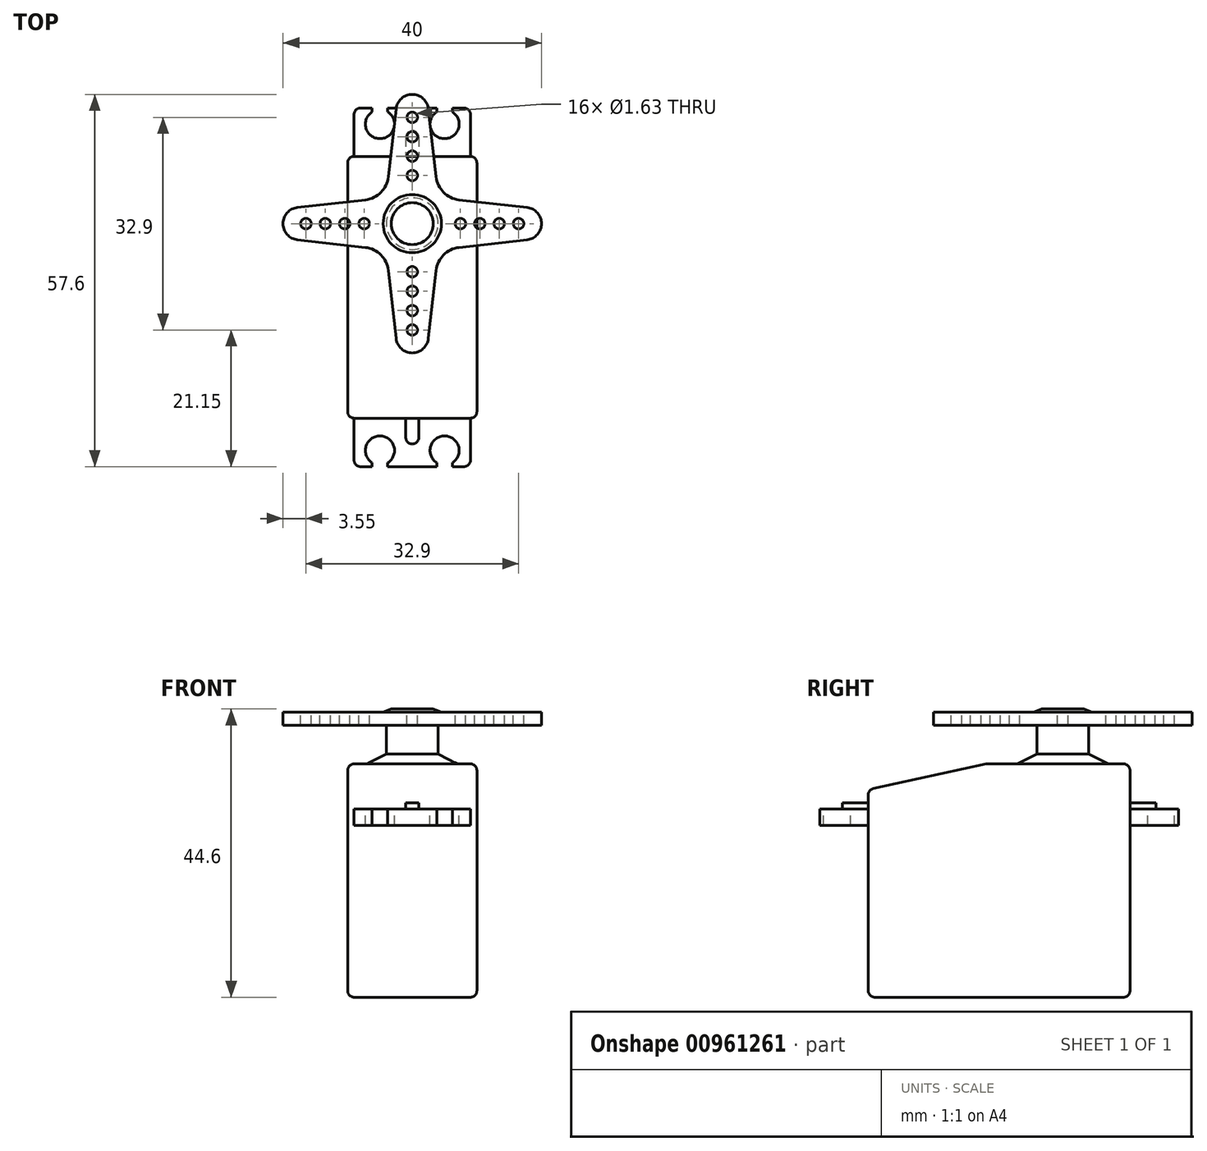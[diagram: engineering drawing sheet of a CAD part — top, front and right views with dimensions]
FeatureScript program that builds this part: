
annotation { "Feature Type Name" : "Feature", "Feature Type Description" : "" }
export const myFeature = defineFeature(function(context is Context, id is Id, definition is map)
    precondition{}
    {
        {
            var Q0;
            Q0=qCreatedBy(makeId("Right.planeOp"),FACE);
            var sketch = newSketch(context, id + "F0", { "sketchPlane" : qUnion([Q0])});
            skLineSegment(sketch, "E0.bottom", {"start": v(-20.25, 0) * mm, "end": v(20.25, 0) * mm});
            skLineSegment(sketch, "E0.top", {"start": v(-20.25, 36.1) * mm, "end": v(20.25, 36.1) * mm});
            skLineSegment(sketch, "E0.left", {"start": v(-20.25, 0) * mm, "end": v(-20.25, 36.1) * mm});
            skLineSegment(sketch, "E0.right", {"start": v(20.25, 0) * mm, "end": v(20.25, 36.1) * mm});
            skLineSegment(sketch, "E1.bottom", {"start": v(20.25, 29.1) * mm, "end": v(27.75, 29.1) * mm});
            skLineSegment(sketch, "E1.top", {"start": v(20.25, 26.6) * mm, "end": v(27.75, 26.6) * mm});
            skLineSegment(sketch, "E1.left", {"start": v(20.25, 29.1) * mm, "end": v(20.25, 26.6) * mm});
            skLineSegment(sketch, "E1.right", {"start": v(27.75, 29.1) * mm, "end": v(27.75, 26.6) * mm});
            skLineSegment(sketch, "E2.bottom", {"start": v(0, 36.1) * mm, "end": v(0, 36.1) * mm});
            skLineSegment(sketch, "E2.top", {"start": v(0, 0) * mm, "end": v(0, 0) * mm});
            skLineSegment(sketch, "E2.left", {"start": v(0, 36.1) * mm, "end": v(0, 0) * mm, "construction": true});
            skLineSegment(sketch, "E2.right", {"start": v(0, 36.1) * mm, "end": v(0, 0) * mm, "construction": true});
            skLineSegment(sketch, "E3.MirrorCS", {"start": v(-20.25, 29.1) * mm, "end": v(-27.75, 29.1) * mm});
            skLineSegment(sketch, "E4.MirrorCS", {"start": v(-27.75, 29.1) * mm, "end": v(-27.75, 26.6) * mm});
            skLineSegment(sketch, "E5.MirrorCS", {"start": v(-20.25, 26.6) * mm, "end": v(-27.75, 26.6) * mm});
            skLineSegment(sketch, "E6.MirrorCS", {"start": v(-20.25, 29.1) * mm, "end": v(-20.25, 26.6) * mm});
            skLineSegment(sketch, "E7", {"start": v(-20.25, 32.1) * mm, "end": v(-1.95, 36.1) * mm});
            skSolve(sketch);
        }
        {
            var Q0;
            {var subQ3=sQuery(id+"F0.wireOp",EDGE,"E0.bottom");Q0=makeQuery(id+"F0.imprint","IMPRINT",FACE,{"disambiguationData":[TD([[makeQuery(id+"F0.imprint","IMPRINT",EDGE,{"derivedFrom":subQ3}),1.0]])]});}
            extrude(context, id + "F1", {"entities" : qUnion([Q0]), "depth" : 20 * mm, "hasSecondDirection" : true, "secondDirectionOppositeDirection" : true, "secondDirectionDepth" : 25 * mm, "symmetric" : true});
        }
        {
            var Q0;
            Q0=makeQuery(id+"F0.imprint","IMPRINT",FACE,{"disambiguationData":[TD([[makeQuery(id+"F0.imprint","IMPRINT",EDGE,{"derivedFrom":sQuery(id+"F0.wireOp",EDGE,"E3.MirrorCS")}),1.0]])]});
            var Q1;
            Q1=makeQuery(id+"F0.imprint","IMPRINT",FACE,{"disambiguationData":[TD([[makeQuery(id+"F0.imprint","IMPRINT",EDGE,{"derivedFrom":sQuery(id+"F0.wireOp",EDGE,"E1.bottom")}),-1.0]])]});
            extrude(context, id + "F2", {"entities" : qUnion([Q0, Q1]), "operationType" : NewBodyOperationType.ADD, "depth" : 18 * mm, "symmetric" : true});
        }
        {
            var Q0;
            Q0=makeQuery(id+"F2.opExtrude","SWEPT_FACE",FACE,{"disambiguationData":[OSD([sQuery(id+"F0.wireOp",EDGE,"E3.MirrorCS")])]});
            var sketch = newSketch(context, id + "F3", { "sketchPlane" : qUnion([Q0])});
            skLineSegment(sketch, "E8.0", {"start": v(-10, -20.25) * mm, "end": v(-10, -1.95) * mm, "construction": true});
            skLineSegment(sketch, "E9.0", {"start": v(-10, -1.95) * mm, "end": v(-10, 20.25) * mm, "construction": true});
            skLineSegment(sketch, "E10.0", {"start": v(10, 20.25) * mm, "end": v(-10, 20.25) * mm, "construction": true});
            skLineSegment(sketch, "E11.0", {"start": v(10, -1.95) * mm, "end": v(10, 20.25) * mm, "construction": true});
            skLineSegment(sketch, "E12.0", {"start": v(10, -20.25) * mm, "end": v(10, -1.95) * mm, "construction": true});
            skLineSegment(sketch, "E13.0", {"start": v(10, -20.25) * mm, "end": v(-10, -20.25) * mm, "construction": true});
            skLineSegment(sketch, "E14", {"start": v(-10, -20.25) * mm, "end": v(10, 20.25) * mm, "construction": true});
            skLineSegment(sketch, "E15", {"start": v(-10, 20.25) * mm, "end": v(10, -20.25) * mm, "construction": true});
            skLineSegment(sketch, "E16", {"start": v(-10, 0) * mm, "end": v(10, 0) * mm, "construction": true});
            skPoint(sketch, "E16.endSnap0", {"position": v(0, 0) * mm});
            skLineSegment(sketch, "E17", {"start": v(0, -20.25) * mm, "end": v(0, 20.25) * mm, "construction": true});
            skCircle(sketch, "E18", {"center": v(-5, -25.25) * mm, "radius": 2.25 * mm});
            skLineSegment(sketch, "E19", {"start": v(-6.2, -27.75) * mm, "end": v(-3.8, -27.75) * mm});
            skLineSegment(sketch, "E20", {"start": v(-3.8, -27.75) * mm, "end": v(-3.8, -27.15) * mm});
            skLineSegment(sketch, "E21", {"start": v(-6.2, -27.75) * mm, "end": v(-6.2, -27.15) * mm});
            skLineSegment(sketch, "E22.MirrorCS", {"start": v(-6.2, 27.75) * mm, "end": v(-6.2, 27.15) * mm});
            skLineSegment(sketch, "E23.MirrorCS", {"start": v(-6.2, 27.75) * mm, "end": v(-3.8, 27.75) * mm});
            skLineSegment(sketch, "E24.MirrorCS", {"start": v(-3.8, 27.75) * mm, "end": v(-3.8, 27.15) * mm});
            skCircle(sketch, "E25.MirrorC", {"center": v(-5, 25.25) * mm, "radius": 2.25 * mm});
            skLineSegment(sketch, "E26.MirrorCS", {"start": v(3.8, -27.75) * mm, "end": v(3.8, -27.15) * mm});
            skLineSegment(sketch, "E27.MirrorCS", {"start": v(3.8, 27.75) * mm, "end": v(3.8, 27.15) * mm});
            skLineSegment(sketch, "E28.MirrorCS", {"start": v(6.2, 27.75) * mm, "end": v(6.2, 27.15) * mm});
            skLineSegment(sketch, "E29.MirrorCS", {"start": v(6.2, -27.75) * mm, "end": v(6.2, -27.15) * mm});
            skLineSegment(sketch, "E30.MirrorCS", {"start": v(6.2, 27.75) * mm, "end": v(3.8, 27.75) * mm});
            skLineSegment(sketch, "E31.MirrorCS", {"start": v(6.2, -27.75) * mm, "end": v(3.8, -27.75) * mm});
            skCircle(sketch, "E32.MirrorC", {"center": v(5, 25.25) * mm, "radius": 2.25 * mm});
            skCircle(sketch, "E33.MirrorC", {"center": v(5, -25.25) * mm, "radius": 2.25 * mm});
            skSolve(sketch);
        }
        {
            var Q0;
            Q0=qSketchRegion(id+"F3",true);
            extrude(context, id + "F4", {"entities" : qUnion([Q0]), "operationType" : NewBodyOperationType.REMOVE, "oppositeDirection" : true, "depth" : 25 * mm});
        }
        {
            var Q0;
            Q0=makeQuery(id+"F2.opExtrude","SWEPT_FACE",FACE,{"disambiguationData":[OSD([sQuery(id+"F0.wireOp",EDGE,"E3.MirrorCS")])]});
            var sketch = newSketch(context, id + "F5", { "sketchPlane" : qUnion([Q0])});
            skLineSegment(sketch, "E34.0", {"start": v(10, -20.25) * mm, "end": v(-10, -20.25) * mm, "construction": true});
            skLineSegment(sketch, "E35.0", {"start": v(10, 20.25) * mm, "end": v(-10, 20.25) * mm, "construction": true});
            skLineSegment(sketch, "E36", {"start": v(0, -20.25) * mm, "end": v(0, 20.25) * mm, "construction": true});
            skLineSegment(sketch, "E37.rect.bottom", {"start": v(1, 23.25) * mm, "end": v(-1, 23.25) * mm});
            skLineSegment(sketch, "E37.rect.top", {"start": v(1, -23.25) * mm, "end": v(-1, -23.25) * mm});
            skLineSegment(sketch, "E37.rect.left", {"start": v(1, 23.25) * mm, "end": v(1, -23.25) * mm});
            skLineSegment(sketch, "E37.rect.right", {"start": v(-1, 23.25) * mm, "end": v(-1, -23.25) * mm});
            skPoint(sketch, "E37.rect.middle", {"position": v(0, 0) * mm});
            skArc(sketch, "E38", {"start": v(1, 23.25) * mm, "mid": v(0, 24.25) * mm, "end": v(-1, 23.25) * mm});
            skArc(sketch, "E39", {"start": v(-1, -23.25) * mm, "mid": v(0, -24.25) * mm, "end": v(1, -23.25) * mm});
            skPoint(sketch, "E40", {"position": v(0, 24.25) * mm});
            skSolve(sketch);
        }
        {
            var Q0;
            Q0=qSketchRegion(id+"F5",true);
            extrude(context, id + "F6", {"entities" : qUnion([Q0]), "operationType" : NewBodyOperationType.ADD, "depth" : 1 * mm});
        }
        {
            var Q0;
            Q0=qCreatedBy(makeId("Right.planeOp"),FACE);
            var sketch = newSketch(context, id + "F7", { "sketchPlane" : qUnion([Q0])});
            skLineSegment(sketch, "E41.0", {"start": v(-1.95, 36.1) * mm, "end": v(20.25, 36.1) * mm, "construction": true});
            skLineSegment(sketch, "E42.0", {"start": v(-20.25, 0) * mm, "end": v(-20.25, 32.1) * mm, "construction": true});
            skLineSegment(sketch, "E43.0", {"start": v(20.25, 0) * mm, "end": v(20.25, 36.1) * mm, "construction": true});
            skLineSegment(sketch, "E44", {"start": v(9.85, 53.58) * mm, "end": v(9.85, 24.34) * mm, "construction": true});
            skLineSegment(sketch, "E45", {"start": v(16.85, 36.1) * mm, "end": v(13.85, 37.6) * mm});
            skLineSegment(sketch, "E46", {"start": v(13.85, 37.6) * mm, "end": v(13.85, 42.1) * mm});
            skLineSegment(sketch, "E47", {"start": v(13.85, 42.1) * mm, "end": v(29.85, 42.1) * mm});
            skLineSegment(sketch, "E48", {"start": v(29.85, 42.1) * mm, "end": v(29.85, 44.1) * mm});
            skLineSegment(sketch, "E49", {"start": v(29.85, 44.1) * mm, "end": v(14.35, 44.1) * mm});
            skLineSegment(sketch, "E50", {"start": v(14.35, 44.1) * mm, "end": v(13.1, 44.6) * mm});
            skLineSegment(sketch, "E51", {"start": v(13.1, 44.6) * mm, "end": v(9.85, 44.6) * mm});
            skLineSegment(sketch, "E52", {"start": v(9.85, 44.6) * mm, "end": v(9.85, 36.1) * mm});
            skLineSegment(sketch, "E53", {"start": v(9.85, 36.1) * mm, "end": v(16.85, 36.1) * mm});
            skSolve(sketch);
        }
        {
            var Q0;
            Q0=qSketchRegion(id+"F7",true);
            var Q1;
            Q1=sQuery(id+"F7.wireOp",EDGE,"E44");
            revolve(context, id + "F8", {"operationType" : NewBodyOperationType.ADD, "entities" : qUnion([Q0]), "axis" : qUnion([Q1]), "revolveType" : RevolveType.FULL});
        }
        {
            var Q0;
            Q0=makeQuery(id+"F8.opRevolve","SWEPT_FACE",FACE,{"disambiguationData":[OSD([sQuery(id+"F7.wireOp",EDGE,"E49")])]});
            var sketch = newSketch(context, id + "F9", { "sketchPlane" : qUnion([Q0])});
            skPoint(sketch, "E54", {"position": v(0, 9.85) * mm});
            skCircle(sketch, "E55", {"center": v(0, 17.3) * mm, "radius": 0.81 * mm});
            skCircle(sketch, "E56", {"center": v(0, 20.3) * mm, "radius": 0.81 * mm});
            skCircle(sketch, "E57", {"center": v(0, 23.3) * mm, "radius": 0.81 * mm});
            skCircle(sketch, "E58", {"center": v(0, 26.3) * mm, "radius": 0.81 * mm});
            skCircle(sketch, "E59.1.0", {"center": v(-16.45, 9.85) * mm, "radius": 0.81 * mm});
            skCircle(sketch, "E59.1.1", {"center": v(-13.45, 9.85) * mm, "radius": 0.81 * mm});
            skCircle(sketch, "E59.1.2", {"center": v(-10.45, 9.85) * mm, "radius": 0.81 * mm});
            skCircle(sketch, "E59.1.3", {"center": v(-7.45, 9.85) * mm, "radius": 0.81 * mm});
            skCircle(sketch, "E59.2.0", {"center": v(0, -6.6) * mm, "radius": 0.81 * mm});
            skCircle(sketch, "E59.2.1", {"center": v(0, -3.6) * mm, "radius": 0.81 * mm});
            skCircle(sketch, "E59.2.2", {"center": v(0, -0.6) * mm, "radius": 0.81 * mm});
            skCircle(sketch, "E59.2.3", {"center": v(0, 2.4) * mm, "radius": 0.81 * mm});
            skCircle(sketch, "E59.3.0", {"center": v(16.45, 9.85) * mm, "radius": 0.81 * mm});
            skCircle(sketch, "E59.3.1", {"center": v(13.45, 9.85) * mm, "radius": 0.81 * mm});
            skCircle(sketch, "E59.3.2", {"center": v(10.45, 9.85) * mm, "radius": 0.81 * mm});
            skCircle(sketch, "E59.3.3", {"center": v(7.45, 9.85) * mm, "radius": 0.81 * mm});
            skSolve(sketch);
        }
        {
            var Q0;
            Q0=qSketchRegion(id+"F9",true);
            extrude(context, id + "F10", {"entities" : qUnion([Q0]), "operationType" : NewBodyOperationType.REMOVE, "endBound" : BoundingType.UP_TO_NEXT, "oppositeDirection" : true, "depth" : 25 * mm});
        }
        {
            var Q0;
            Q0=makeQuery(id+"F8.opRevolve","SWEPT_FACE",FACE,{"disambiguationData":[OSD([sQuery(id+"F7.wireOp",EDGE,"E49")])]});
            var sketch = newSketch(context, id + "F11", { "sketchPlane" : qUnion([Q0])});
            skPoint(sketch, "E60", {"position": v(0, 9.85) * mm});
            skLineSegment(sketch, "E61", {"start": v(0, 9.85) * mm, "end": v(0, 29.85) * mm, "construction": true});
            skLineSegment(sketch, "E62", {"start": v(0, 9.85) * mm, "end": v(-14.14, 24) * mm, "construction": true});
            skLineSegment(sketch, "E63", {"start": v(0, 9.85) * mm, "end": v(14.14, 24) * mm, "construction": true});
            skLineSegment(sketch, "E64", {"start": v(-3.69, 17.1) * mm, "end": v(-2.5, 27.62) * mm});
            skArc(sketch, "E65", {"start": v(0, 29.85) * mm, "mid": v(-1.68, 29.21) * mm, "end": v(-2.5, 27.62) * mm});
            skArc(sketch, "E66", {"start": v(-4.84, 14.7) * mm, "mid": v(-4.06, 15.8) * mm, "end": v(-3.69, 17.1) * mm});
            skArc(sketch, "E67.MirrorCS", {"start": v(4.84, 14.7) * mm, "mid": v(4.06, 15.8) * mm, "end": v(3.69, 17.1) * mm});
            skLineSegment(sketch, "E68.MirrorCS", {"start": v(3.69, 17.1) * mm, "end": v(2.5, 27.62) * mm});
            skArc(sketch, "E69.MirrorCS", {"start": v(0, 29.85) * mm, "mid": v(1.68, 29.21) * mm, "end": v(2.5, 27.62) * mm});
            skArc(sketch, "E70.1.0", {"start": v(-4.84, 5) * mm, "mid": v(-5.95, 5.79) * mm, "end": v(-7.24, 6.16) * mm});
            skLineSegment(sketch, "E70.1.1", {"start": v(-7.24, 6.16) * mm, "end": v(-17.77, 7.35) * mm});
            skArc(sketch, "E70.1.2", {"start": v(-20, 9.85) * mm, "mid": v(-19.36, 8.17) * mm, "end": v(-17.77, 7.35) * mm});
            skArc(sketch, "E70.1.3", {"start": v(-20, 9.85) * mm, "mid": v(-19.36, 11.53) * mm, "end": v(-17.77, 12.35) * mm});
            skLineSegment(sketch, "E70.1.4", {"start": v(-7.24, 13.54) * mm, "end": v(-17.77, 12.35) * mm});
            skArc(sketch, "E70.1.5", {"start": v(-4.84, 14.7) * mm, "mid": v(-5.95, 13.91) * mm, "end": v(-7.24, 13.54) * mm});
            skArc(sketch, "E70.2.0", {"start": v(4.84, 5) * mm, "mid": v(4.06, 3.9) * mm, "end": v(3.69, 2.6) * mm});
            skLineSegment(sketch, "E70.2.1", {"start": v(3.69, 2.6) * mm, "end": v(2.5, -7.92) * mm});
            skArc(sketch, "E70.2.2", {"start": v(0, -10.15) * mm, "mid": v(1.68, -9.51) * mm, "end": v(2.5, -7.92) * mm});
            skArc(sketch, "E70.2.3", {"start": v(0, -10.15) * mm, "mid": v(-1.68, -9.51) * mm, "end": v(-2.5, -7.92) * mm});
            skLineSegment(sketch, "E70.2.4", {"start": v(-3.69, 2.6) * mm, "end": v(-2.5, -7.92) * mm});
            skArc(sketch, "E70.2.5", {"start": v(-4.84, 5) * mm, "mid": v(-4.06, 3.9) * mm, "end": v(-3.69, 2.6) * mm});
            skArc(sketch, "E70.3.0", {"start": v(4.84, 14.7) * mm, "mid": v(5.95, 13.91) * mm, "end": v(7.24, 13.54) * mm});
            skLineSegment(sketch, "E70.3.1", {"start": v(7.24, 13.54) * mm, "end": v(17.77, 12.35) * mm});
            skArc(sketch, "E70.3.2", {"start": v(20, 9.85) * mm, "mid": v(19.36, 11.53) * mm, "end": v(17.77, 12.35) * mm});
            skArc(sketch, "E70.3.3", {"start": v(20, 9.85) * mm, "mid": v(19.36, 8.17) * mm, "end": v(17.77, 7.35) * mm});
            skLineSegment(sketch, "E70.3.4", {"start": v(7.24, 6.16) * mm, "end": v(17.77, 7.35) * mm});
            skArc(sketch, "E70.3.5", {"start": v(4.84, 5) * mm, "mid": v(5.95, 5.79) * mm, "end": v(7.24, 6.16) * mm});
            skCircle(sketch, "E71", {"center": v(0, 9.85) * mm, "radius": 26.3 * mm});
            skSolve(sketch);
        }
        {
            var Q0;
            Q0=qSketchRegion(id+"F11",true);
            var Q1;
            Q1=makeQuery(id+"F8.opRevolve","SWEPT_FACE",FACE,{"disambiguationData":[OSD([sQuery(id+"F7.wireOp",EDGE,"E47")])]});
            extrude(context, id + "F12", {"entities" : qUnion([Q0]), "operationType" : NewBodyOperationType.REMOVE, "endBound" : BoundingType.UP_TO_SURFACE, "oppositeDirection" : true, "endBoundEntityFace" : qUnion([Q1]), "depth" : 25 * mm});
        }
        {
            var Q0;
            Q0=makeQuery(id+"F1.opExtrude","CAP_FACE",FACE,{"disambiguationData":[OSD([sQuery(id+"F0.wireOp",EDGE,"E0.bottom"),sQuery(id+"F0.wireOp",EDGE,"E0.top"),sQuery(id+"F0.wireOp",EDGE,"E0.left"),sQuery(id+"F0.wireOp",EDGE,"E0.right"),sQuery(id+"F0.wireOp",EDGE,"E1.left"),sQuery(id+"F0.wireOp",EDGE,"E6.MirrorCS"),sQuery(id+"F0.wireOp",EDGE,"E7")])],"isStart":false});
            var Q1;
            Q1=makeQuery(id+"F1.opExtrude","CAP_FACE",FACE,{"disambiguationData":[OSD([sQuery(id+"F0.wireOp",EDGE,"E0.bottom"),sQuery(id+"F0.wireOp",EDGE,"E0.top"),sQuery(id+"F0.wireOp",EDGE,"E0.left"),sQuery(id+"F0.wireOp",EDGE,"E0.right"),sQuery(id+"F0.wireOp",EDGE,"E1.left"),sQuery(id+"F0.wireOp",EDGE,"E6.MirrorCS"),sQuery(id+"F0.wireOp",EDGE,"E7")])],"isStart":true});
            var Q2;
            Q2=makeQuery(id+"F1.opExtrude","SWEPT_FACE",FACE,{"disambiguationData":[OSD([sQuery(id+"F0.wireOp",EDGE,"E0.bottom")])]});
            var Q3;
            Q3=makeQuery(id+"F1.opExtrude","SWEPT_FACE",FACE,{"disambiguationData":[OSD([sQuery(id+"F0.wireOp",EDGE,"E7")])]});
            var Q4;
            Q4=makeQuery(id+"F1.opExtrude","SWEPT_FACE",FACE,{"disambiguationData":[OSD([sQuery(id+"F0.wireOp",EDGE,"E0.top")])]});
            var Q5;
            Q5=makeQuery(id+"F2.opExtrude","CAP_EDGE",EDGE,{"disambiguationData":[OSD([sQuery(id+"F0.wireOp",EDGE,"E4.MirrorCS")])],"isStart":false});
            var Q6;
            Q6=makeQuery(id+"F2.opExtrude","CAP_EDGE",EDGE,{"disambiguationData":[OSD([sQuery(id+"F0.wireOp",EDGE,"E4.MirrorCS")])],"isStart":true});
            var Q7;
            Q7=makeQuery(id+"F2.opExtrude","CAP_EDGE",EDGE,{"disambiguationData":[OSD([sQuery(id+"F0.wireOp",EDGE,"E1.right")])],"isStart":false});
            var Q8;
            Q8=makeQuery(id+"F2.opExtrude","CAP_EDGE",EDGE,{"disambiguationData":[OSD([sQuery(id+"F0.wireOp",EDGE,"E1.right")])],"isStart":true});
            fillet(context, id + "F13", {"entities" : qUnion([Q0, Q1, Q2, Q3, Q4, Q5, Q6, Q7, Q8]), "radius" : 1 * mm, "tangentPropagation" : true, "allowEdgeOverflow" : false});
        }
    });
